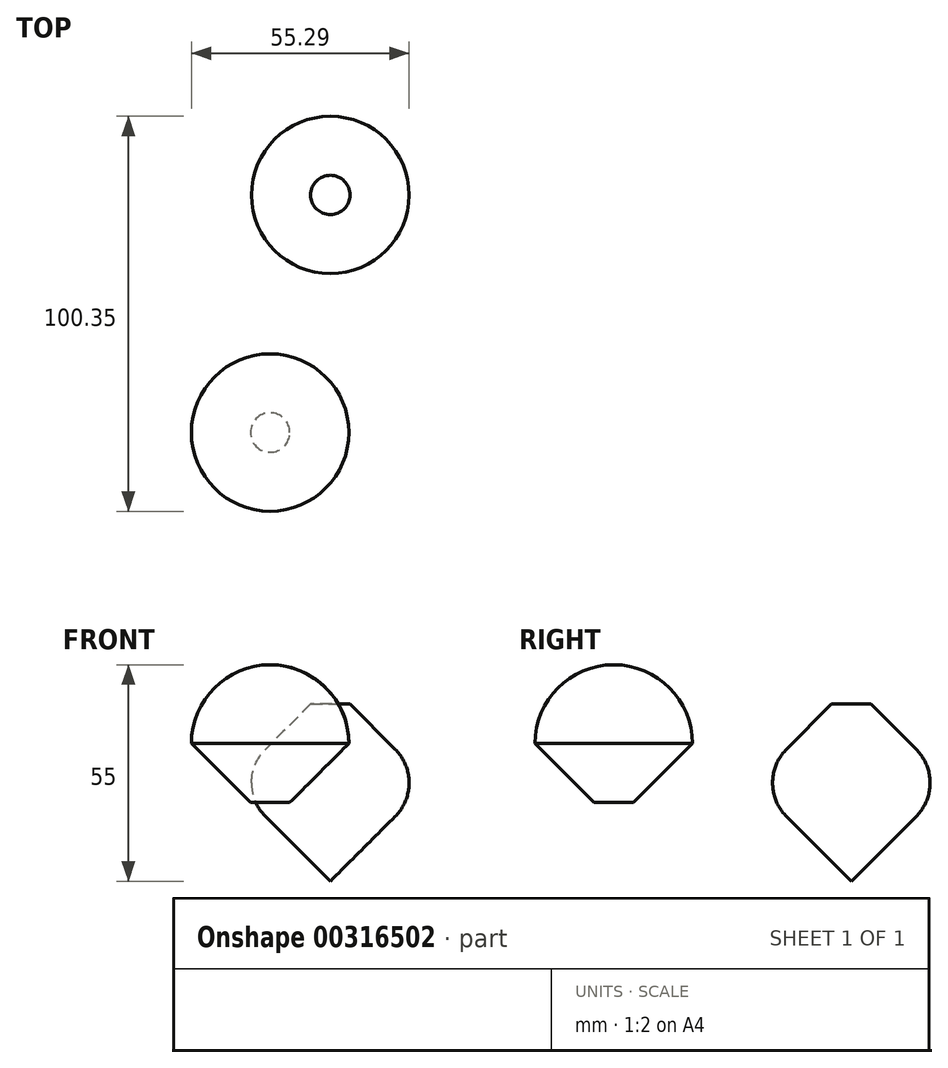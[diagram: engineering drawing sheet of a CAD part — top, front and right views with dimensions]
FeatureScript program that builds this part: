
annotation { "Feature Type Name" : "Feature", "Feature Type Description" : "" }
export const myFeature = defineFeature(function(context is Context, id is Id, definition is map)
    precondition{}
    {
        {
            var Q0;
            Q0=qCreatedBy(makeId("Top.planeOp"),FACE);
            var sketch = newSketch(context, id + "F0", { "sketchPlane" : qUnion([Q0])});
            skCircle(sketch, "E0", {"center": v(-105.15, 83.3) * mm, "radius": 20 * mm});
            skSolve(sketch);
        }
        {
            var Q0;
            Q0=makeQuery(id+"F0.imprint","IMPRINT",FACE,{"disambiguationData":[TD([[makeQuery(id+"F0.imprint","IMPRINT",EDGE,{"derivedFrom":sQuery(id+"F0.wireOp",EDGE,"E0")}),1.0]])]});
            extrude(context, id + "F1", {"entities" : qUnion([Q0]), "depth" : 15 * mm});
        }
        {
            var Q0;
            Q0=makeQuery(id+"F1.opExtrude","CAP_FACE",FACE,{"disambiguationData":[OSD([sQuery(id+"F0.wireOp",EDGE,"E0")])],"isStart":true});
            extrude(context, id + "F2", {"entities" : qUnion([Q0]), "operationType" : NewBodyOperationType.ADD, "depth" : 30 * mm});
        }
        {
            var Q0;
            Q0=makeQuery(id+"F2.opExtrude","CAP_EDGE",EDGE,{"disambiguationData":[OSD([sQuery(id+"F0.wireOp",EDGE,"E0")])],"isStart":false});
            chamfer(context, id + "F3", {"entities" : qUnion([Q0]), "width" : 20 * mm, "tangentPropagation" : true});
        }
        {
            var Q0;
            Q0=qCreatedBy(makeId("Top.planeOp"),FACE);
            var sketch = newSketch(context, id + "F4", { "sketchPlane" : qUnion([Q0])});
            skCircle(sketch, "E1", {"center": v(-120.44, 22.95) * mm, "radius": 20 * mm});
            skSolve(sketch);
        }
        {
            var Q0;
            Q0=makeQuery(id+"F4.imprint","IMPRINT",FACE,{"disambiguationData":[TD([[makeQuery(id+"F4.imprint","IMPRINT",EDGE,{"derivedFrom":sQuery(id+"F4.wireOp",EDGE,"E1")}),1.0]])]});
            extrude(context, id + "F5", {"entities" : qUnion([Q0]), "depth" : 25 * mm});
        }
        {
            var Q0;
            Q0=makeQuery(id+"F5.opExtrude","CAP_EDGE",EDGE,{"disambiguationData":[OSD([sQuery(id+"F4.wireOp",EDGE,"E1")])],"isStart":false});
            fillet(context, id + "F6", {"entities" : qUnion([Q0]), "radius" : 20 * mm, "tangentPropagation" : true, "allowEdgeOverflow" : false});
        }
        {
            var Q0;
            Q0=makeQuery(id+"F5.opExtrude","CAP_FACE",FACE,{"disambiguationData":[OSD([sQuery(id+"F4.wireOp",EDGE,"E1")])],"isStart":true});
            extrude(context, id + "F7", {"entities" : qUnion([Q0]), "operationType" : NewBodyOperationType.ADD, "depth" : 10 * mm});
        }
        {
            var Q0;
            Q0=makeQuery(id+"F7.opExtrude","CAP_EDGE",EDGE,{"disambiguationData":[OSD([sQuery(id+"F4.wireOp",EDGE,"E1")])],"isStart":false});
            chamfer(context, id + "F8", {"entities" : qUnion([Q0]), "width" : 15 * mm, "tangentPropagation" : true});
        }
        {
            var Q0;
            Q0=makeQuery(id+"F1.opExtrude","CAP_EDGE",EDGE,{"disambiguationData":[OSD([sQuery(id+"F0.wireOp",EDGE,"E0")])],"isStart":false});
            chamfer(context, id + "F9", {"entities" : qUnion([Q0]), "width" : 15 * mm, "tangentPropagation" : true});
        }
        {
            var Q0;
            {var subQ0=sQuery(id+"F0.wireOp",EDGE,"E0");Q0=makeQuery(id+"F9.opChamfer","BLEND_EDGE",EDGE,{"blendedFrom":[makeQuery(id+"F1.opExtrude","CAP_EDGE",EDGE,{"disambiguationData":[OSD([subQ0])],"isStart":false}),makeQuery(id+"F2.boolean.opBoolean","MERGE",FACE,{"derivedFrom":[makeQuery(id+"F1.opExtrude","SWEPT_FACE",FACE,{"disambiguationData":[OSD([subQ0])]}),makeQuery(id+"F2.opExtrude","SWEPT_FACE",FACE,{"disambiguationData":[OSD([subQ0])]})]})],"blendedInto":[makeQuery(id+"F2.boolean.opBoolean","MERGE",FACE,{"derivedFrom":[makeQuery(id+"F1.opExtrude","SWEPT_FACE",FACE,{"disambiguationData":[OSD([subQ0])]}),makeQuery(id+"F2.opExtrude","SWEPT_FACE",FACE,{"disambiguationData":[OSD([subQ0])]})]})]});}
            var Q1;
            {var subQ0=sQuery(id+"F0.wireOp",EDGE,"E0");Q1=makeQuery(id+"F3.opChamfer","BLEND_EDGE",EDGE,{"blendedFrom":[makeQuery(id+"F2.opExtrude","CAP_EDGE",EDGE,{"disambiguationData":[OSD([subQ0])],"isStart":false}),makeQuery(id+"F2.boolean.opBoolean","MERGE",FACE,{"derivedFrom":[makeQuery(id+"F1.opExtrude","SWEPT_FACE",FACE,{"disambiguationData":[OSD([subQ0])]}),makeQuery(id+"F2.opExtrude","SWEPT_FACE",FACE,{"disambiguationData":[OSD([subQ0])]})]})],"blendedInto":[makeQuery(id+"F2.boolean.opBoolean","MERGE",FACE,{"derivedFrom":[makeQuery(id+"F1.opExtrude","SWEPT_FACE",FACE,{"disambiguationData":[OSD([subQ0])]}),makeQuery(id+"F2.opExtrude","SWEPT_FACE",FACE,{"disambiguationData":[OSD([subQ0])]})]})]});}
            fillet(context, id + "F10", {"entities" : qUnion([Q0, Q1]), "tangentPropagation" : true, "radius" : 12 * mm, "defaultsChanged" : true, "vertexSettings" : [], "allowEdgeOverflow" : false});
        }
    });
